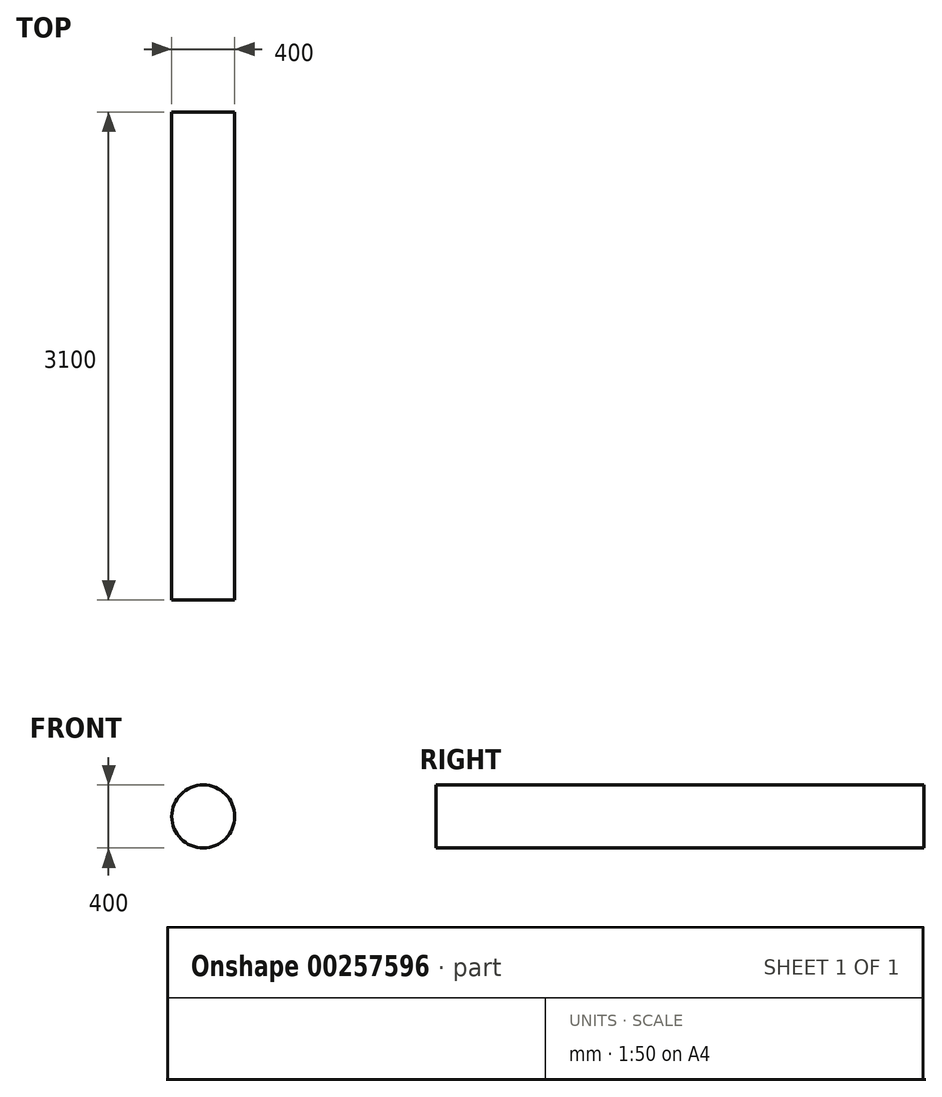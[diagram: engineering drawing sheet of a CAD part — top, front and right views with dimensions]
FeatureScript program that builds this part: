
annotation { "Feature Type Name" : "Feature", "Feature Type Description" : "" }
export const myFeature = defineFeature(function(context is Context, id is Id, definition is map)
    precondition{}
    {
        {
            var Q0;
            Q0=qCreatedBy(makeId("Front.planeOp"),FACE);
            var sketch = newSketch(context, id + "F0", { "sketchPlane" : qUnion([Q0])});
            skCircle(sketch, "E0", {"center": v(0, 0) * mm, "radius": 200 * mm});
            skSolve(sketch);
        }
        {
            var Q0;
            Q0 = qSketchRegion(id + "F0", true);
            extrude(context, id + "F1", {"entities" : qUnion([Q0]), "depth" : 3100 * mm});
        }
    });
